# Revit family: Electronics_Masking-Generators_Biamp_Cambridge_Sound-Masking-System_DS1092__
name_source: partatom
category: Communication Devices
units: mm (PartAtom-declared; Revit-internal decimal feet)

## family parameters
Cut with Voids When Loaded = No
Host = Face
Maintain Annotation Orientation = No
OmniClass Number = 23.85.10.11
OmniClass Title = Audio Information, Sound Signals
Part Type = Normal
Room Calculation Point = No
Round Connector Dimension = Use Diameter
Shared = No

## types (1)
- DS1092
    Apparent Load = 135 VA
    Connector Description = 120 VAC, 60 Hz, 135 watts
    Default Elevation = 4' - 0"
    Depth = 0' - 11 1/2"
    Description = Dynasound® DS1092 Sound Masking, Paging and Music System for 70.7 Volt Speakers
    Generator = Digital white noise generator
    Height = 0' - 3 1/2"
    Housing Material = Biamp - Metal - Dark Gray
    Manufacturer = Biamp
    Max Power Consumption = 135 W
    Mixer = Internal sound masking, music input and paging input
    Model = DS1092
    Number of Poles = 1
    Output = 40 W, 70.7 V
    Power Factor = 1
    Product Documentation Link = https://downloads.biamp.com
    Product Page URL = https://www.biamp.com
    Product data url = https://www.bimobject.com
    Shipping Weight = 10.00 lbf
    Tuning = Low-pass filter on front panel
    URL = https://www.biamp.com
    Voltage = 120 V
    Width = 0' - 9"

## geometry (parser evidence)
native form markers: Sweep x2
no freeform markers — native parametric forms only
